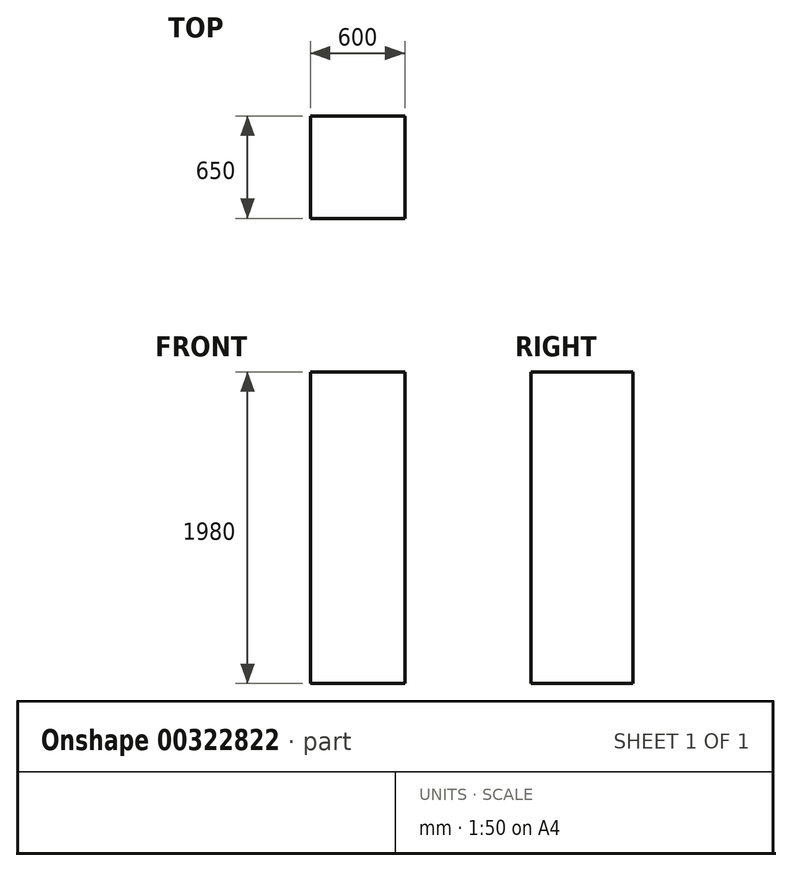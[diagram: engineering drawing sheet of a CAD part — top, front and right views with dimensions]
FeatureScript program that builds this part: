
annotation { "Feature Type Name" : "Feature", "Feature Type Description" : "" }
export const myFeature = defineFeature(function(context is Context, id is Id, definition is map)
    precondition{}
    {
        {
            var Q0;
            Q0=qCreatedBy(makeId("Top.planeOp"),FACE);
            var sketch = newSketch(context, id + "F0", { "sketchPlane" : qUnion([Q0])});
            skLineSegment(sketch, "E0.bottom", {"start": v(300, -325) * mm, "end": v(-300, -325) * mm});
            skLineSegment(sketch, "E0.top", {"start": v(300, 325) * mm, "end": v(-300, 325) * mm});
            skLineSegment(sketch, "E0.left", {"start": v(300, -325) * mm, "end": v(300, 325) * mm});
            skLineSegment(sketch, "E0.right", {"start": v(-300, -325) * mm, "end": v(-300, 325) * mm});
            skPoint(sketch, "E0.middle", {"position": v(0, 0) * mm});
            skSolve(sketch);
        }
        {
            var Q0;
            Q0=makeQuery(id+"F0.imprint","IMPRINT",FACE,{"disambiguationData":[TD([[makeQuery(id+"F0.imprint","IMPRINT",EDGE,{"derivedFrom":sQuery(id+"F0.wireOp",EDGE,"E0.bottom")}),-1.0]])]});
            extrude(context, id + "F1", {"entities" : qUnion([Q0]), "depth" : 1980 * mm});
        }
    });
